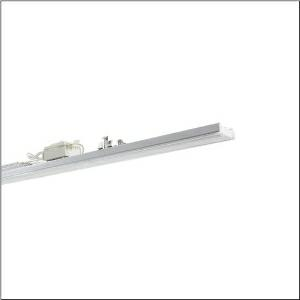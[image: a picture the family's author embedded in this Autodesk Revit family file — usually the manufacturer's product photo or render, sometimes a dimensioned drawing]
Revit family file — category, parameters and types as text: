
# Revit family: licross_r__11_recessed_ho_51tl12mn4exm_8c12
name_source: partatom
category: Lighting Fixtures
units: mm (PartAtom-declared; Revit-internal decimal feet)

## family parameters
Cut with Voids When Loaded = No
Host = Face
Light Source = No
Part Type = Normal
Room Calculation Point = No
Round Connector Dimension = Use Diameter
Shared = No

## types (1)
- --- (1 x LED, 14100 lm, 74.5 W, 4000K)
    Apparent Load = 75 VA
    CIE Flux Codes = 66 91 98 100 100
    Color Rendering = 80
    Color Temperature = 4000K
    Default Elevation = 1800 mm
    Description = Licross® 11 Recessed HO, luminaire insert, of sheet steel, coil coated, white, length: 1.500mm, width: 66mm, height: 67mm, LED rated luminous flux: 14.100lm, light colour: 840, control gear: ON/OFF Multilumen, with plug, 3-pole, with phase selection, mains connection: 220..240V, AC, 50/60Hz, rated input power: 75W, internal wiring halogen-free, primary optical cover: cover, of PMMA, light emission: direct distribution, primary light characteristic: symmetric, protection rating (complete): IP40, insulation class (complete): insulation class I (protective earthing), certification: CE, ENEC, VDE, UKCA, protection symbol: D if used in an environment without relevant dust loads with corresponding accessories, impact resistance: IK06, permissible ambient temperature for indoor applications: -35..+35°C, corresponds to IFS (International Featured Standards) requirements for safety and quality in the food industry, reducing of maximum allowable ambient temperature of 5°C with ceiling mounting, packaging unit: 1 piece
    Height = 58 mm
    Lamp = 1 x LED
    Lamp Light Flux = 14100 lm
    Lamp Power = 74.5 W
    Lamp count = 1
    Length = 1500 mm
    Luminous efficacy = 189 lm/W
    Manufacturer = Siteco
    ModVariant = No
    Model = 51TL12MN4EXM
    Mounting Place = Ceiling
    Mounting Type = Pendant
    Number of Poles = 1
    OnlyDefault = Yes
    Power Factor = 1
    Product Name = Licross® 11 Recessed HO
    Product group = luminaire insert | ceiling pendant
    ProductGroupID = 902
    Protection Class = Protection class I
    Protection Degree = IP 40
    RLX_Detail_Level = 1
    RLX_Emergency_Light_Flux = 0 lm
    RLX_Emergency_Type = 0
    RLX_Emergency_Type_DB = No
    RlxData = <blob elided: 22177 chars, md5=4c3ab7b0>
    Socket = socket
    Standby Power = 0 W
    System Light Flux = 14100 lm
    System Power = 75 W
    Type Comments = factory setting: luminous flux: 100 % | (A | C | E) | 174 mA
    Type Image = l_1296930.jpg
    URL = http://relux.com
    VarID = @adj_106639
    Voltage = 0 V
    Weight = 0.00 kg
    Width = 66 mm

## geometry (parser evidence)
native form markers: Blend x4, Sweep x10
no freeform markers — native parametric forms only
